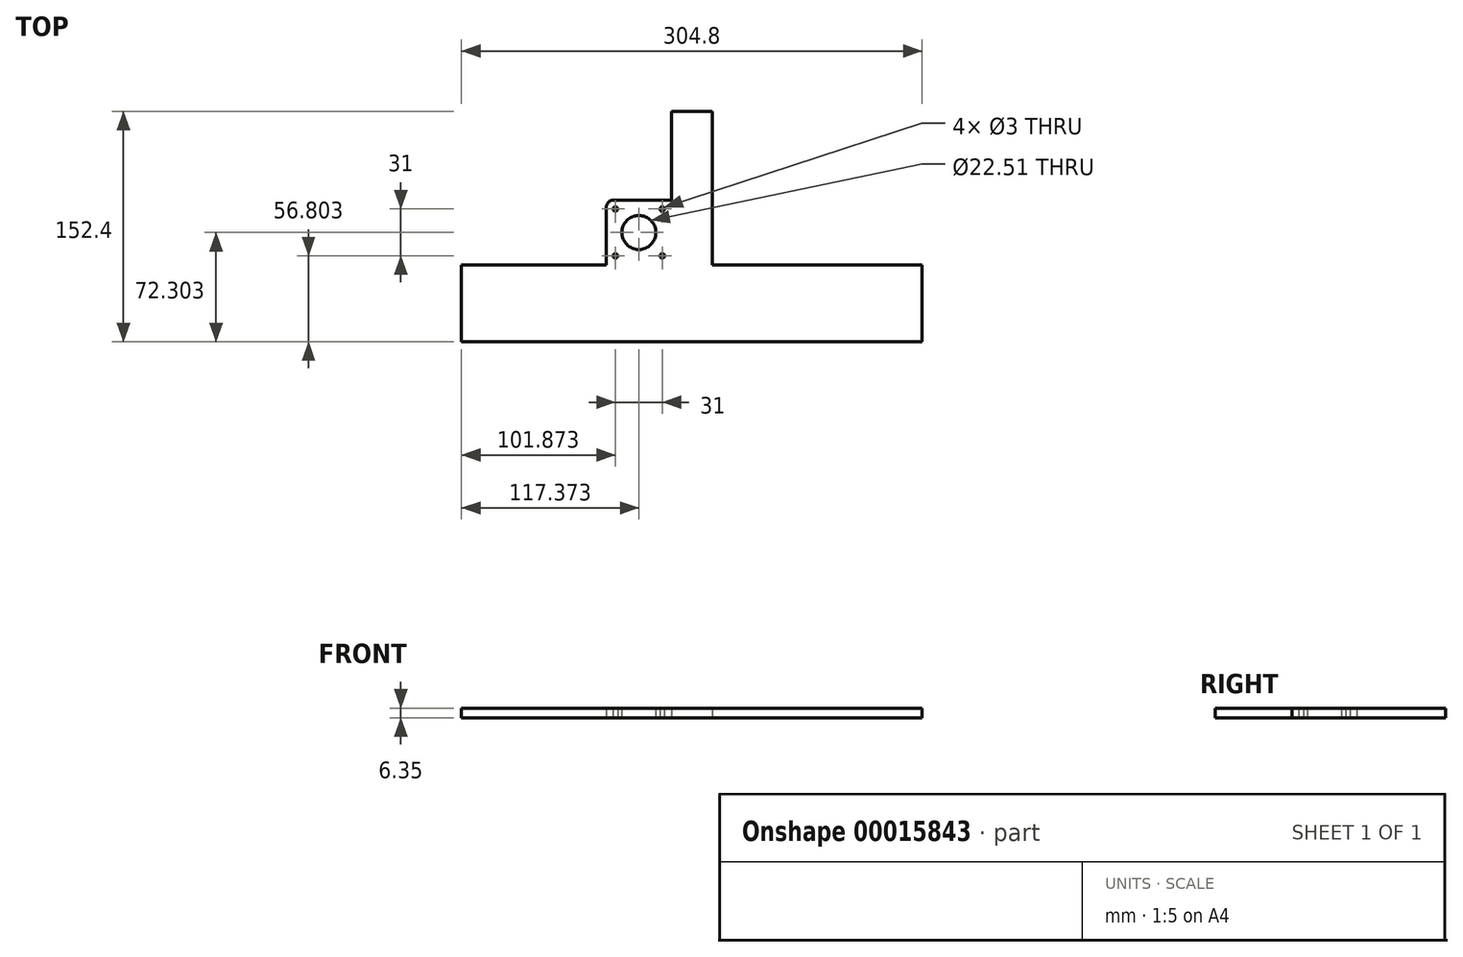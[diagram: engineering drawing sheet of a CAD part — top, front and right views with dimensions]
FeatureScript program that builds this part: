
annotation { "Feature Type Name" : "Feature", "Feature Type Description" : "" }
export const myFeature = defineFeature(function(context is Context, id is Id, definition is map)
    precondition{}
    {
        {
            var Q0;
            Q0=qCreatedBy(makeId("Top.planeOp"),FACE);
            var sketch = newSketch(context, id + "F0", { "sketchPlane" : qUnion([Q0])});
            skLineSegment(sketch, "E0.top", {"start": v(0, 43) * mm, "end": v(43, 43) * mm});
            skLineSegment(sketch, "E0.left", {"start": v(0, 0) * mm, "end": v(0, 43) * mm});
            skLineSegment(sketch, "E1.top", {"start": v(-95.87, -50.8) * mm, "end": v(208.93, -50.8) * mm});
            skLineSegment(sketch, "E1.left", {"start": v(-95.87, 0) * mm, "end": v(-95.87, -50.8) * mm});
            skLineSegment(sketch, "E1.right", {"start": v(208.93, 0) * mm, "end": v(208.93, -50.8) * mm});
            skLineSegment(sketch, "E2.top", {"start": v(70.06, 101.6) * mm, "end": v(43, 101.6) * mm});
            skLineSegment(sketch, "E2.left", {"start": v(70.06, 0) * mm, "end": v(70.06, 101.6) * mm});
            skLineSegment(sketch, "E3", {"start": v(43, 43) * mm, "end": v(43, 101.6) * mm});
            skLineSegment(sketch, "E4", {"start": v(0, 0) * mm, "end": v(-95.87, 0) * mm});
            skLineSegment(sketch, "E5", {"start": v(70.06, 0) * mm, "end": v(208.93, 0) * mm});
            skLineSegment(sketch, "E6", {"start": v(21.5, 43) * mm, "end": v(21.5, 21.5) * mm});
            skLineSegment(sketch, "E7", {"start": v(21.5, 21.5) * mm, "end": v(0, 21.5) * mm});
            skLineSegment(sketch, "E8.rect.bottom", {"start": v(37, 37) * mm, "end": v(6, 37) * mm, "construction": true});
            skLineSegment(sketch, "E8.rect.top", {"start": v(37, 6) * mm, "end": v(6, 6) * mm, "construction": true});
            skLineSegment(sketch, "E8.rect.left", {"start": v(37, 37) * mm, "end": v(37, 6) * mm, "construction": true});
            skLineSegment(sketch, "E8.rect.right", {"start": v(6, 37) * mm, "end": v(6, 6) * mm, "construction": true});
            skPoint(sketch, "E8.rect.middle", {"position": v(21.5, 21.5) * mm});
            skCircle(sketch, "E9", {"center": v(21.5, 21.5) * mm, "radius": 11.25 * mm});
            skCircle(sketch, "E10", {"center": v(37, 37) * mm, "radius": 1.5 * mm});
            skCircle(sketch, "E11", {"center": v(37, 6) * mm, "radius": 1.5 * mm});
            skCircle(sketch, "E12", {"center": v(6, 6) * mm, "radius": 1.5 * mm});
            skCircle(sketch, "E13", {"center": v(6, 37) * mm, "radius": 1.5 * mm});
            skLineSegment(sketch, "E14", {"start": v(56.53, 101.6) * mm, "end": v(56.53, -50.8) * mm});
            skSolve(sketch);
        }
        {
            var Q0;
            Q0 = qSketchRegion(id + "F0", true);
            extrude(context, id + "F1", {"entities" : qUnion([Q0]), "depth" : 6.35 * mm});
        }
        {
            var Q0;
            Q0=makeQuery(id+"F1.opExtrude","SWEPT_EDGE",EDGE,{"disambiguationData":[OSD([sQuery(id+"F0.wireOp",EDGE,"E0.top"),sQuery(id+"F0.wireOp",EDGE,"E0.left")])]});
            fillet(context, id + "F2", {"entities" : qUnion([Q0]), "radius" : 5.08 * mm, "tangentPropagation" : true, "allowEdgeOverflow" : false});
        }
    });
